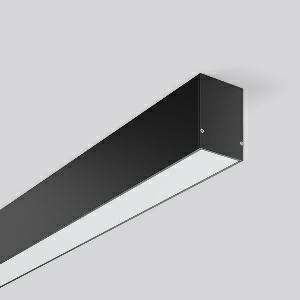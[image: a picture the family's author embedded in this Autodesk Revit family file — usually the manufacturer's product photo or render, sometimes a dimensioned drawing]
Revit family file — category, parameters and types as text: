
# Revit family: less_is_more_50_312308_003_1_76_4cd9
name_source: partatom
category: Lighting Fixtures
units: mm (PartAtom-declared; Revit-internal decimal feet)

## family parameters
Cut with Voids When Loaded = No
Host = Face
Light Source = No
Part Type = Normal
Room Calculation Point = No
Round Connector Dimension = Use Diameter
Shared = No

## types (1)
- LESS IS MORE 50 (1 x LED Modul 840, 4850 lm, 4000)
    Apparent Load = 40 VA
    CIE Flux Codes = 48 79 95 100 100
    Color Rendering = 80
    Color Temperature = 4000
    Default Elevation = 1800 mm
    Description = Series: LESS IS MORE 50
Linear ceiling and wall luminaire for aesthetically sophisticated lighting. Housing: extruded aluminium profile, powder-coated. End cap aluminium powder-coated. Diffuser made of non-yellowing plastic (PMMA), opal. Suitable for Ceiling mounting. LED unit with integrated converter interchangeable and removable. Suitable for through-wiring. With sensors or as a safety luminaire on request. 
Colour: deep black, matt (RAL 9005)
Length: 1687 mm
Width: 57 mm
Height: 75 mm
Lamp: LED
Socket: without socket
Colour temperature: 4000K
Colour rendering index (CRI): 80
System power: 40 W
Rated luminous flux: 4850 lm
Luminous efficiency: 121 lm/W
Control gear: Converter, dimmable, DALI
Protection class: I
Type of protection: IP 20
    Height = 75 mm
    Lamp = 1 x LED Modul 840
    Lamp Light Flux = 4850 lm
    Lamp count = 1
    Length = 1687 mm
    Lifetime = 50000 h
    Luminous efficacy = 121 lm/W
    Manufacturer = RZB
    ModVariant = No
    Model = 312308.003.1.76
    Mounting Place = Ceiling
    Mounting Type = Surface mounted
    Number of Poles = 1
    OnlyDefault = Yes
    Power Factor = 1
    Product Name = LESS IS MORE 50
    Product group = Surface mounted ceiling LED linear luminaires
    ProductGroupID = 312
    Protection Class = Protection class I
    Protection Degree = IP 20
    RLX_Detail_Level = 1
    RLX_Emergency_Light_Flux = 0 lm
    RLX_Emergency_Type = 0
    RLX_Emergency_Type_DB = No
    RlxData = <blob elided: 28873 chars, md5=f5ae8758>
    Socket = socket
    Standby Power = 0 W
    System Light Flux = 4850 lm
    System Power = 40 W
    Type Comments = Product without accessories
    Type Image = 312306.003.jpg
    URL = http://relux.com
    VarID = ---
    Voltage = 230 V
    Voltage Range = 220-240 V
    Weight = 0.00 kg
    Width = 57 mm

## geometry (parser evidence)
native form markers: Blend x4, Sweep x9
no freeform markers — native parametric forms only
